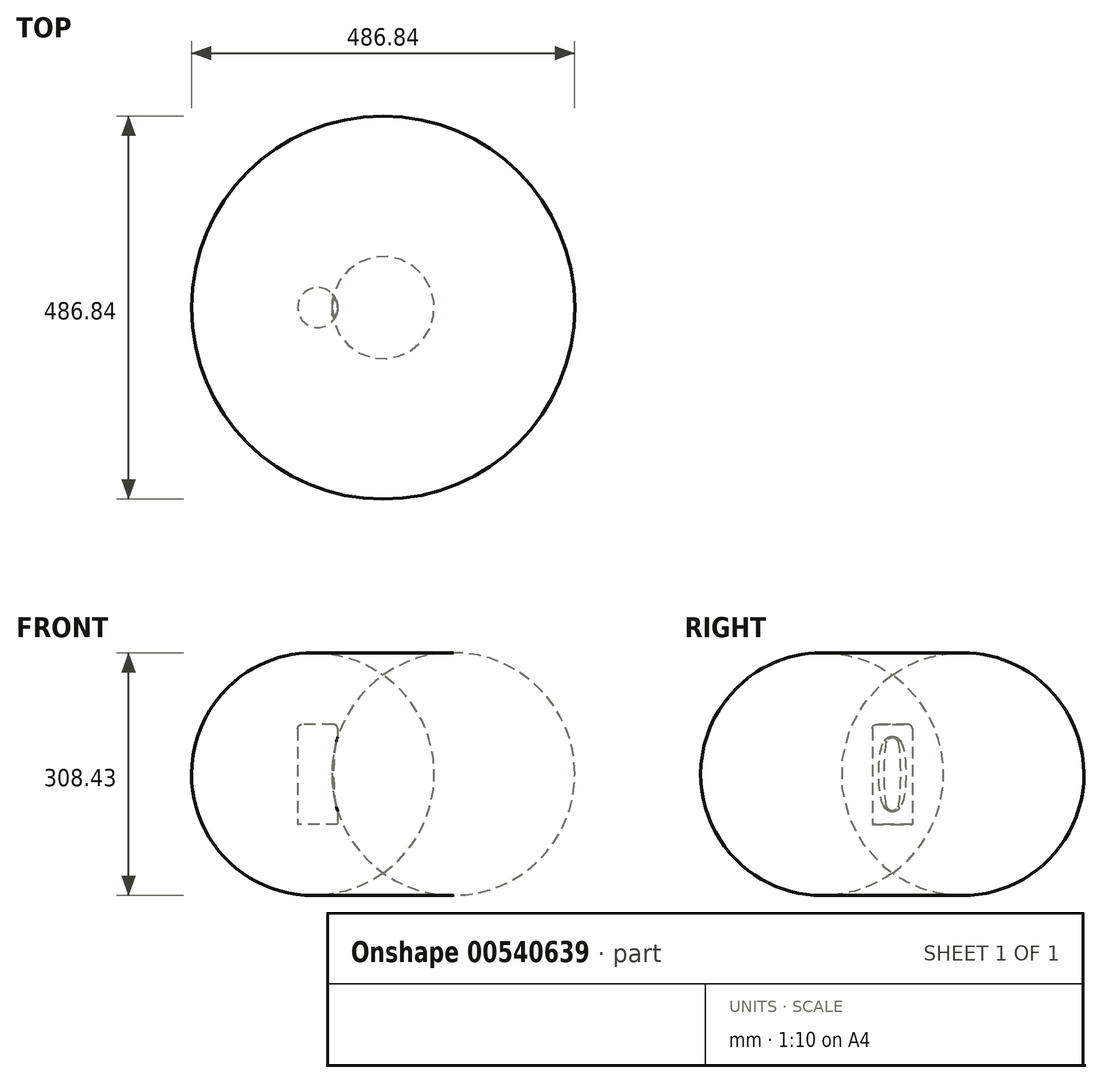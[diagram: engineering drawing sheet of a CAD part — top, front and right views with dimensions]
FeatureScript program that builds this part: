
annotation { "Feature Type Name" : "Feature", "Feature Type Description" : "" }
export const myFeature = defineFeature(function(context is Context, id is Id, definition is map)
    precondition{}
    {
        {
            var Q0;
            Q0=qCreatedBy(makeId("Front.planeOp"),FACE);
            var sketch = newSketch(context, id + "F0", { "sketchPlane" : qUnion([Q0])});
            skLineSegment(sketch, "E0", {"start": v(0, 0) * mm, "end": v(0, 110.1) * mm, "construction": true});
            skLineSegment(sketch, "E1", {"start": v(0, 26.03) * mm, "end": v(35.2, 26.03) * mm, "construction": true});
            skLineSegment(sketch, "E2", {"start": v(0, 55.05) * mm, "end": v(35.2, 55.05) * mm, "construction": true});
            skSolve(sketch);
        }
        {
            var Q0;
            Q0=qCreatedBy(makeId("Top.planeOp"),FACE);
            var sketch = newSketch(context, id + "F1", { "sketchPlane" : qUnion([Q0])});
            skCircle(sketch, "E3", {"center": v(0, 0) * mm, "radius": 25.4 * mm});
            skSolve(sketch);
        }
        {
            var Q0;
            Q0=qCreatedBy(makeId("Top.planeOp"),FACE);
            cPlane(context, id + "F2", {"entities" : qUnion([Q0]), "cplaneType" : CPlaneType.OFFSET, "offset" : 50.8 * mm, "width" : 152.4 * mm, "height" : 152.4 * mm});
        }
        {
            var Q0;
            Q0=qCreatedBy(id+"F2.planeOp",FACE);
            cPlane(context, id + "F3", {"entities" : qUnion([Q0]), "cplaneType" : CPlaneType.OFFSET, "offset" : 101.6 * mm, "width" : 152.4 * mm, "height" : 152.4 * mm});
        }
        {
            var Q0;
            Q0=qCreatedBy(id+"F2.planeOp",FACE);
            var sketch = newSketch(context, id + "F4", { "sketchPlane" : qUnion([Q0])});
            skCircle(sketch, "E4.0", {"center": v(0, 0) * mm, "radius": 25.4 * mm});
            skSolve(sketch);
        }
        {
            var Q0;
            Q0=makeQuery(id+"F1.imprint","IMPRINT",FACE,{"disambiguationData":[TD([[makeQuery(id+"F1.imprint","IMPRINT",EDGE,{"derivedFrom":sQuery(id+"F1.wireOp",EDGE,"E3")}),1.0]])]});
            extrude(context, id + "F5", {"entities" : qUnion([Q0]), "depth" : 127 * mm, "offsetDistance" : 25.4 * mm});
        }
        {
            var Q0;
            Q0=makeQuery(id+"F5.opExtrude","CAP_EDGE",EDGE,{"disambiguationData":[OSD([sQuery(id+"F1.wireOp",EDGE,"E3")])],"isStart":false});
            fillet(context, id + "F6", {"entities" : qUnion([Q0]), "radius" : 5.08 * mm, "tangentPropagation" : true, "allowEdgeOverflow" : false});
        }
        {
            var Q0;
            Q0=qCreatedBy(makeId("Front.planeOp"),FACE);
            var sketch = newSketch(context, id + "F7", { "sketchPlane" : qUnion([Q0])});
            skArc(sketch, "E5", {"start": v(83.04, 189.88) * mm, "mid": v(18.03, 64.08) * mm, "end": v(83.04, -61.73) * mm});
            skLineSegment(sketch, "E6", {"start": v(83.04, 189.88) * mm, "end": v(83.04, -61.73) * mm});
            skSolve(sketch);
        }
        {
            var Q0;
            Q0=makeQuery(id+"F7.imprint","IMPRINT",FACE,{"disambiguationData":[TD([[makeQuery(id+"F7.imprint","IMPRINT",EDGE,{"derivedFrom":sQuery(id+"F7.wireOp",EDGE,"E5")}),1.0]])]});
            extrude(context, id + "F8", {"entities" : qUnion([Q0]), "operationType" : NewBodyOperationType.REMOVE, "endBound" : BoundingType.SYMMETRIC, "oppositeDirection" : true, "depth" : 25.4 * mm, "offsetDistance" : 25.4 * mm});
        }
        {
            var Q0;
            Q0=makeQuery(id+"F8.boolean.opBoolean","COPY",EDGE,{"derivedFrom":makeQuery(id+"F8.opExtrude","CAP_EDGE",EDGE,{"disambiguationData":[OSD([sQuery(id+"F7.wireOp",EDGE,"E5")])],"isStart":false})});
            var Q1;
            Q1=makeQuery(id+"F8.boolean.opBoolean","COPY",EDGE,{"derivedFrom":makeQuery(id+"F8.opExtrude","CAP_EDGE",EDGE,{"disambiguationData":[OSD([sQuery(id+"F7.wireOp",EDGE,"E5")])],"isStart":true})});
            fillet(context, id + "F9", {"entities" : qUnion([Q0, Q1]), "radius" : 5.08 * mm, "tangentPropagation" : true, "allowEdgeOverflow" : false});
        }
        {
            var Q0;
            Q0=makeQuery(id+"F9.opFillet","BLEND_EDGE",EDGE,{"blendedFrom":[makeQuery(id+"F8.boolean.opBoolean","COPY",EDGE,{"derivedFrom":makeQuery(id+"F8.opExtrude","CAP_EDGE",EDGE,{"disambiguationData":[OSD([sQuery(id+"F7.wireOp",EDGE,"E5")])],"isStart":true})}),makeQuery(id+"F5.opExtrude","SWEPT_FACE",FACE,{"disambiguationData":[OSD([sQuery(id+"F1.wireOp",EDGE,"E3")])]})],"blendedInto":[makeQuery(id+"F5.opExtrude","SWEPT_FACE",FACE,{"disambiguationData":[OSD([sQuery(id+"F1.wireOp",EDGE,"E3")])]})]});
            fillet(context, id + "F10", {"entities" : qUnion([Q0]), "radius" : 5.08 * mm, "tangentPropagation" : true, "allowEdgeOverflow" : false});
        }
        {
            var Q0;
            Q0=qCreatedBy(makeId("Front.planeOp"),FACE);
            var sketch = newSketch(context, id + "F11", { "sketchPlane" : qUnion([Q0])});
            skCircle(sketch, "E7", {"center": v(19.05, 50.8) * mm, "radius": 4.45 * mm});
            skCircle(sketch, "E8", {"center": v(19.05, 31.75) * mm, "radius": 4.45 * mm});
            skLineSegment(sketch, "E9", {"start": v(0, 50.8) * mm, "end": v(19.05, 50.8) * mm, "construction": true});
            skCircle(sketch, "E10", {"center": v(19.05, 76.2) * mm, "radius": 4.45 * mm});
            skCircle(sketch, "E11", {"center": v(19.05, 95.25) * mm, "radius": 4.45 * mm});
            skLineSegment(sketch, "E12", {"start": v(0, 0) * mm, "end": v(19.05, 0) * mm, "construction": true});
            skSolve(sketch);
        }
        {
            var Q0;
            Q0=makeQuery(id+"F7.imprint","IMPRINT",FACE,{"disambiguationData":[TD([[makeQuery(id+"F7.imprint","IMPRINT",EDGE,{"derivedFrom":sQuery(id+"F7.wireOp",EDGE,"E5")}),1.0]])]});
            var Q1;
            Q1=sQuery(id+"F7.wireOp",EDGE,"E6");
            revolve(context, id + "F12", {"entities" : qUnion([Q0]), "axis" : qUnion([Q1]), "revolveType" : RevolveType.FULL});
        }
    });
